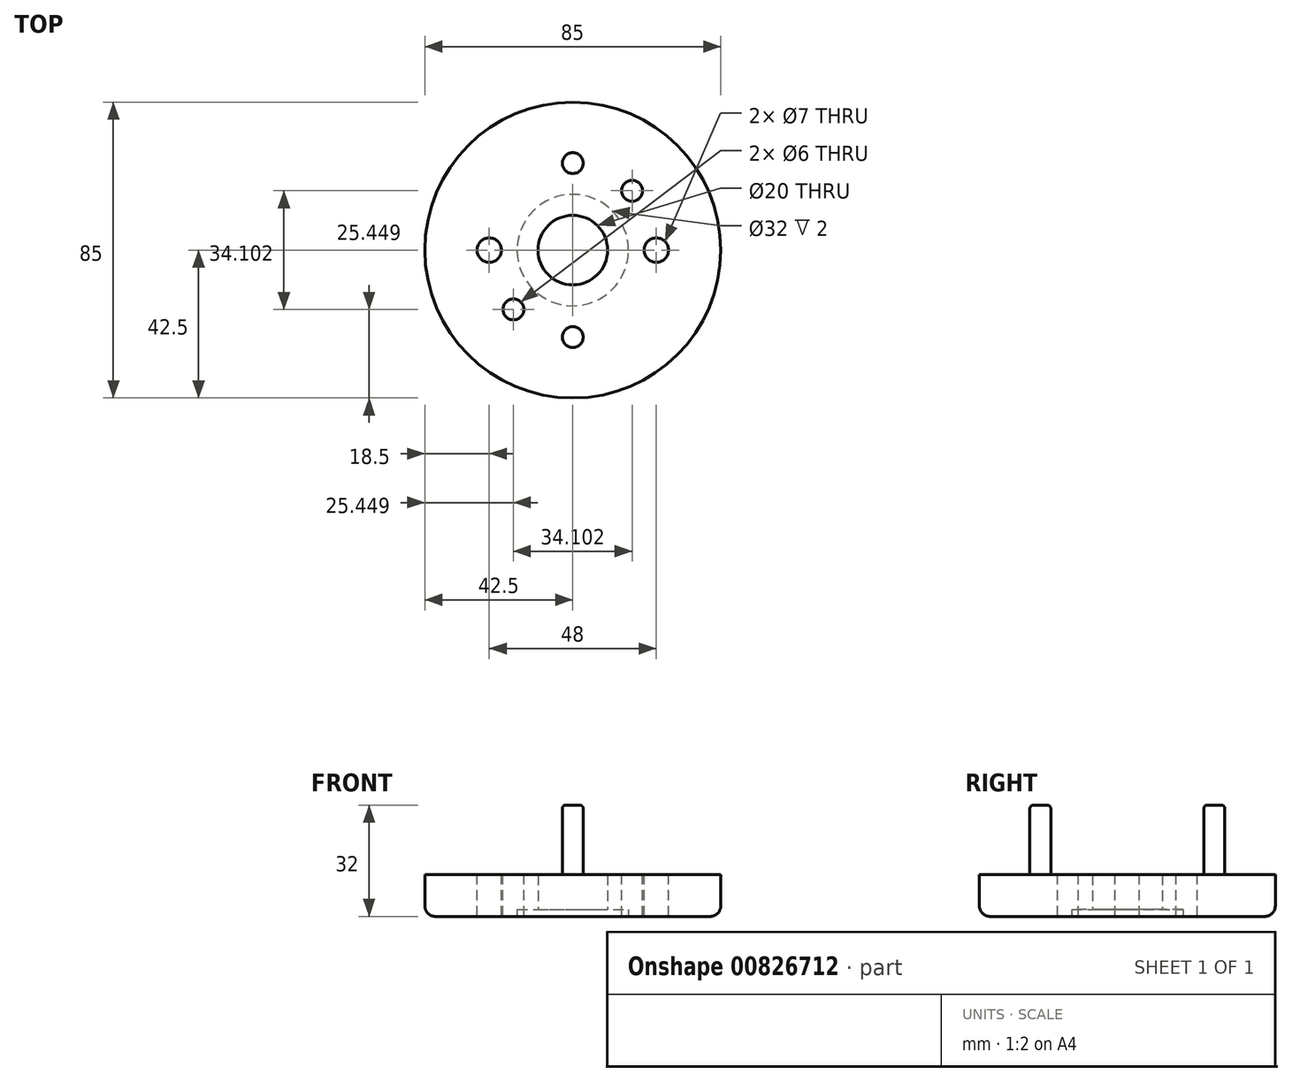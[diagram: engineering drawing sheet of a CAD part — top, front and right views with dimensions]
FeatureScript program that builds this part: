
annotation { "Feature Type Name" : "Feature", "Feature Type Description" : "" }
export const myFeature = defineFeature(function(context is Context, id is Id, definition is map)
    precondition{}
    {
        {
            var Q0;
            Q0=qCreatedBy(makeId("Front.planeOp"),FACE);
            var sketch = newSketch(context, id + "F0", { "sketchPlane" : qUnion([Q0])});
            skPoint(sketch, "E0", {"position": v(-16, 0) * mm});
            skLineSegment(sketch, "E1", {"start": v(-16, 0) * mm, "end": v(-42.5, 0) * mm});
            skLineSegment(sketch, "E2", {"start": v(-16, 0) * mm, "end": v(-16, 2) * mm});
            skLineSegment(sketch, "E3", {"start": v(-16, 2) * mm, "end": v(-10, 2) * mm});
            skLineSegment(sketch, "E4", {"start": v(-10, 2) * mm, "end": v(-10, 12) * mm});
            skLineSegment(sketch, "E5", {"start": v(2.5, 12) * mm, "end": v(-10, 12) * mm});
            skLineSegment(sketch, "E6", {"start": v(-42.5, 0) * mm, "end": v(-42.5, 12) * mm});
            skLineSegment(sketch, "E7", {"start": v(-42.5, 12) * mm, "end": v(2.5, 12) * mm});
            skLineSegment(sketch, "E8", {"start": v(0, 0) * mm, "end": v(0, 39.27) * mm});
            skSolve(sketch);
        }
        {
            var Q0;
            Q0=makeQuery(id+"F0.imprint","IMPRINT",FACE,{"disambiguationData":[TD([[makeQuery(id+"F0.imprint","IMPRINT",EDGE,{"derivedFrom":sQuery(id+"F0.wireOp",EDGE,"E1")}),-1.0]])]});
            var Q1;
            Q1=sQuery(id+"F0.wireOp",EDGE,"E8");
            revolve(context, id + "F1", {"surfaceOperationType" : NewSurfaceOperationType.NEW, "entities" : qUnion([Q0]), "axis" : qUnion([Q1]), "revolveType" : RevolveType.FULL});
        }
        {
            var Q0;
            Q0=makeQuery(id+"F1.opRevolve","SWEPT_EDGE",EDGE,{"disambiguationData":[OSD([sQuery(id+"F0.wireOp",EDGE,"E1"),sQuery(id+"F0.wireOp",EDGE,"E6")])]});
            fillet(context, id + "F2", {"entities" : qUnion([Q0]), "radius" : 3 * mm, "tangentPropagation" : true, "allowEdgeOverflow" : false});
        }
        {
            var Q0;
            Q0=makeQuery(id+"F1.opRevolve","SWEPT_FACE",FACE,{"disambiguationData":[OSD([sQuery(id+"F0.wireOp",EDGE,"E7")])]});
            var sketch = newSketch(context, id + "F3", { "sketchPlane" : qUnion([Q0])});
            skPoint(sketch, "E9", {"position": v(-24, 0) * mm});
            skPoint(sketch, "E10", {"position": v(24, 0) * mm});
            skCircle(sketch, "E11", {"center": v(-24, 0) * mm, "radius": 3.5 * mm});
            skCircle(sketch, "E12", {"center": v(24, 0) * mm, "radius": 3.5 * mm});
            skPoint(sketch, "E13", {"position": v(0, 25) * mm});
            skPoint(sketch, "E14", {"position": v(0, -25) * mm});
            skCircle(sketch, "E15", {"center": v(0, 25) * mm, "radius": 3 * mm});
            skCircle(sketch, "E16", {"center": v(0, -25) * mm, "radius": 3 * mm});
            skSolve(sketch);
        }
        {
            var Q0;
            Q0=makeQuery(id+"F3.imprint","IMPRINT",FACE,{"disambiguationData":[TD([[makeQuery(id+"F3.imprint","IMPRINT",EDGE,{"derivedFrom":sQuery(id+"F3.wireOp",EDGE,"E11")}),1.0]])]});
            var Q1;
            Q1=makeQuery(id+"F3.imprint","IMPRINT",FACE,{"disambiguationData":[TD([[makeQuery(id+"F3.imprint","IMPRINT",EDGE,{"derivedFrom":sQuery(id+"F3.wireOp",EDGE,"E12")}),1.0]])]});
            extrude(context, id + "F4", {"entities" : qUnion([Q0, Q1]), "operationType" : NewBodyOperationType.REMOVE, "oppositeDirection" : true, "depth" : 25 * mm, "offsetDistance" : 25 * mm});
        }
        {
            var Q0;
            Q0=makeQuery(id+"F3.imprint","IMPRINT",FACE,{"disambiguationData":[TD([[makeQuery(id+"F3.imprint","IMPRINT",EDGE,{"derivedFrom":sQuery(id+"F3.wireOp",EDGE,"E16")}),1.0]])]});
            var Q1;
            Q1=makeQuery(id+"F3.imprint","IMPRINT",FACE,{"disambiguationData":[TD([[makeQuery(id+"F3.imprint","IMPRINT",EDGE,{"derivedFrom":sQuery(id+"F3.wireOp",EDGE,"E15")}),1.0]])]});
            extrude(context, id + "F5", {"entities" : qUnion([Q0, Q1]), "operationType" : NewBodyOperationType.ADD, "depth" : 20 * mm, "offsetDistance" : 25 * mm});
        }
        {
            var Q0;
            Q0=makeQuery(id+"F5.opExtrude","CAP_FACE",FACE,{"disambiguationData":[OSD([sQuery(id+"F3.wireOp",EDGE,"E16")])],"isStart":false});
            var Q1;
            Q1=makeQuery(id+"F5.opExtrude","CAP_EDGE",EDGE,{"disambiguationData":[OSD([sQuery(id+"F3.wireOp",EDGE,"E15")])],"isStart":false});
            fillet(context, id + "F6", {"entities" : qUnion([Q0, Q1]), "radius" : 1 * mm, "tangentPropagation" : true, "allowEdgeOverflow" : false});
        }
        {
            var Q0;
            Q0=makeQuery(id+"F3.imprint","IMPRINT",FACE,{"disambiguationData":[TD([[makeQuery(id+"F3.imprint","IMPRINT",EDGE,{"derivedFrom":sQuery(id+"F3.wireOp",EDGE,"E11")}),-1.0]])]});
            var sketch = newSketch(context, id + "F7", { "sketchPlane" : qUnion([Q0])});
            skPoint(sketch, "E17", {"position": v(17.05, 17.05) * mm});
            skPoint(sketch, "E18", {"position": v(-17.05, -17.05) * mm});
            skCircle(sketch, "E19", {"center": v(17.05, 17.05) * mm, "radius": 3 * mm});
            skCircle(sketch, "E20", {"center": v(-17.05, -17.05) * mm, "radius": 3 * mm});
            skSolve(sketch);
        }
        {
            var Q0;
            Q0=makeQuery(id+"F7.imprint","IMPRINT",FACE,{"disambiguationData":[TD([[makeQuery(id+"F7.imprint","IMPRINT",EDGE,{"derivedFrom":sQuery(id+"F7.wireOp",EDGE,"E20")}),1.0]])]});
            var Q1;
            Q1=makeQuery(id+"F7.imprint","IMPRINT",FACE,{"disambiguationData":[TD([[makeQuery(id+"F7.imprint","IMPRINT",EDGE,{"derivedFrom":sQuery(id+"F7.wireOp",EDGE,"E19")}),1.0]])]});
            var Q2;
            Q2=sQuery(id+"F7.wireOp",EDGE,"E19");
            var Q3;
            Q3=sQuery(id+"F7.wireOp",EDGE,"E20");
            extrude(context, id + "F8", {"entities" : qUnion([Q0, Q1]), "operationType" : NewBodyOperationType.REMOVE, "surfaceEntities" : qUnion([Q2, Q3]), "oppositeDirection" : true, "depth" : 25 * mm, "offsetDistance" : 25 * mm});
        }
    });
